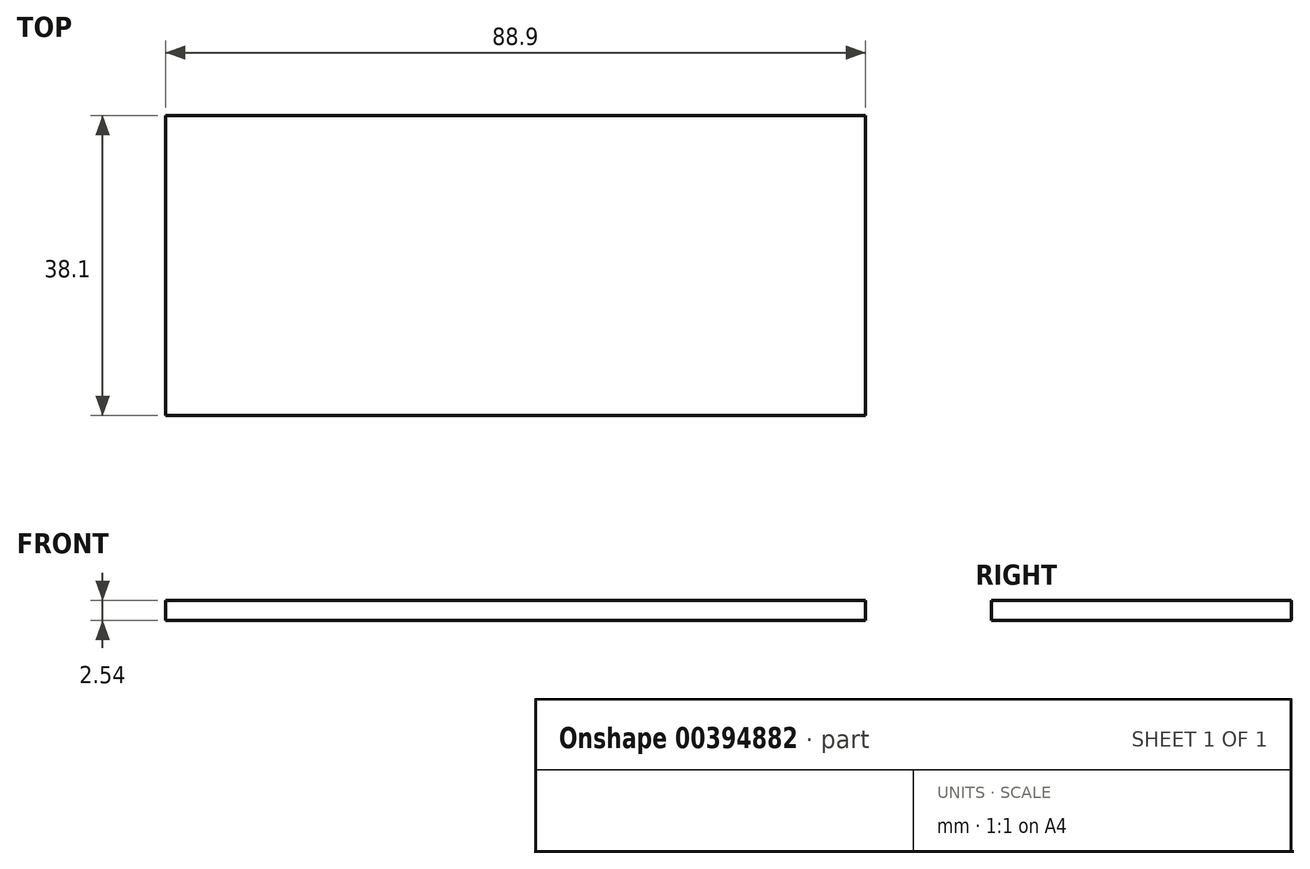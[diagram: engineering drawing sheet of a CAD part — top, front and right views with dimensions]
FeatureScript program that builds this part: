
annotation { "Feature Type Name" : "Feature", "Feature Type Description" : "" }
export const myFeature = defineFeature(function(context is Context, id is Id, definition is map)
    precondition{}
    {
        {
            var Q0;
            Q0=qCreatedBy(makeId("Top.planeOp"),FACE);
            var sketch = newSketch(context, id + "F0", { "sketchPlane" : qUnion([Q0])});
            skLineSegment(sketch, "E0.bottom", {"start": v(0, 0) * mm, "end": v(88.9, 0) * mm});
            skLineSegment(sketch, "E0.top", {"start": v(0, 38.1) * mm, "end": v(88.9, 38.1) * mm});
            skLineSegment(sketch, "E0.left", {"start": v(0, 0) * mm, "end": v(0, 38.1) * mm});
            skLineSegment(sketch, "E0.right", {"start": v(88.9, 0) * mm, "end": v(88.9, 38.1) * mm});
            skSolve(sketch);
        }
        {
            var Q0;
            Q0 = qSketchRegion(id + "F0", true);
            extrude(context, id + "F1", {"entities" : qUnion([Q0]), "depth" : 2.54 * mm});
        }
    });
